# Revit family: Sanitary_Taps-Mixers_AXOR_49410XXX-AXOR-Citterio-C-Bath-spout__
name_source: partatom
category: Plumbing Fixtures
units: mm (PartAtom-declared; Revit-internal decimal feet)

## family parameters
Always vertical = No
Cut with Voids When Loaded = No
OmniClass Number = 23.31.11.00
OmniClass Title = Faucets
Part Type = Normal
Room Calculation Point = No
Round Connector Dimension = Use Diameter
Shared = No
Work Plane-Based = Yes

## types (1)
- Default - please load Revit Family Type Catalog
    Connector Description = Water Inlet 12.7mm
    Default Elevation = 1219 mm
    Description = AXOR Citterio C Bath spout
    Diameter = 13 mm
    Manufacturer = AXOR
    Material = AXOR - Metal - 000 Chrome
    Model = 49410XXX
    Product Guid = ff85053a-0c57-49da-b734-b08e257b1928
    Product Page URL = https://www.axor-design.com
    Product data url = https://bimobject.com
    URL = https://www.axor-design.com
    Version = 1

## geometry (parser evidence)
native form markers: Sweep x2
no freeform markers — native parametric forms only
